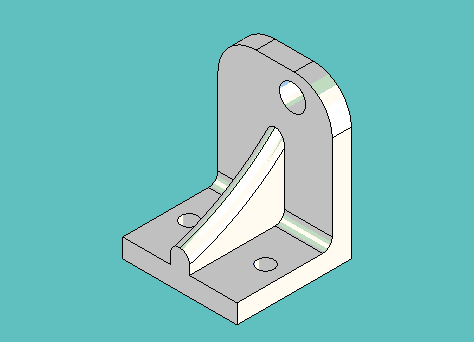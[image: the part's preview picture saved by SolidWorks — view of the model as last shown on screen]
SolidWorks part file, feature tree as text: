
SOLIDWORKS PART (.sldprt)
format: sldprt  version: not decoded by parser v0  size: 809,984 bytes
history: native  units: mm
features: sketch x4, extrude x4, boolean_combine x3, fillet x2, material x1, plane x1 (+11 scaffold rows collapsed)
feature tree (26):
  scaffold x11  (default folders/planes/origin — collapsed)
  material  "Material <not specified>"
  sketch  "Sketch1"  dims[D1=25.4mm D2=25.4mm D3=9.398mm D4=3.175mm D5=19.05mm D6=3.175mm D7=9.398mm D8=1.6002mm D9=19.05mm D10=1.6002mm]
  extrude  "Extrude1"  Depth=19.05mm
  sketch  "Sketch2"  dims[c1.D1=4.3688mm c1.D3=4.3688mm c1.D2=12.446mm c2.D3=21.59mm c2.D4=12.446mm c2.D2=21.59mm]
  extrude  "Extrude2"  [1 undecoded]
  boolean_combine  "Combine1"
  plane  "Plane1"
  sketch  "Sketch3"  dims[c1.D2=38.1mm c1.D1=12.7mm c2.D2=3.175mm c2.D3=3.175mm]
  extrude  "Extrude3"  Depth=1.5875mm
  boolean_combine  "Combine2"
  sketch  "Sketch4"  dims[D1=~2.77622mm D2=11.1125mm D3=6.35mm]
  extrude  "Extrude4"  [1 undecoded]
  boolean_combine  "Combine3"
  fillet  "Fillet1"  Radius=1.5875mm
  fillet  "Fillet2"  Radius=6.35mm
decode coverage: 8 of 13 modeling features carry decoded parameters
note: ~ marks probable driven/reference dimensions
note: 2 parameter values undecoded
note: suppression state not decoded; provenance and decode notes live in map.json
